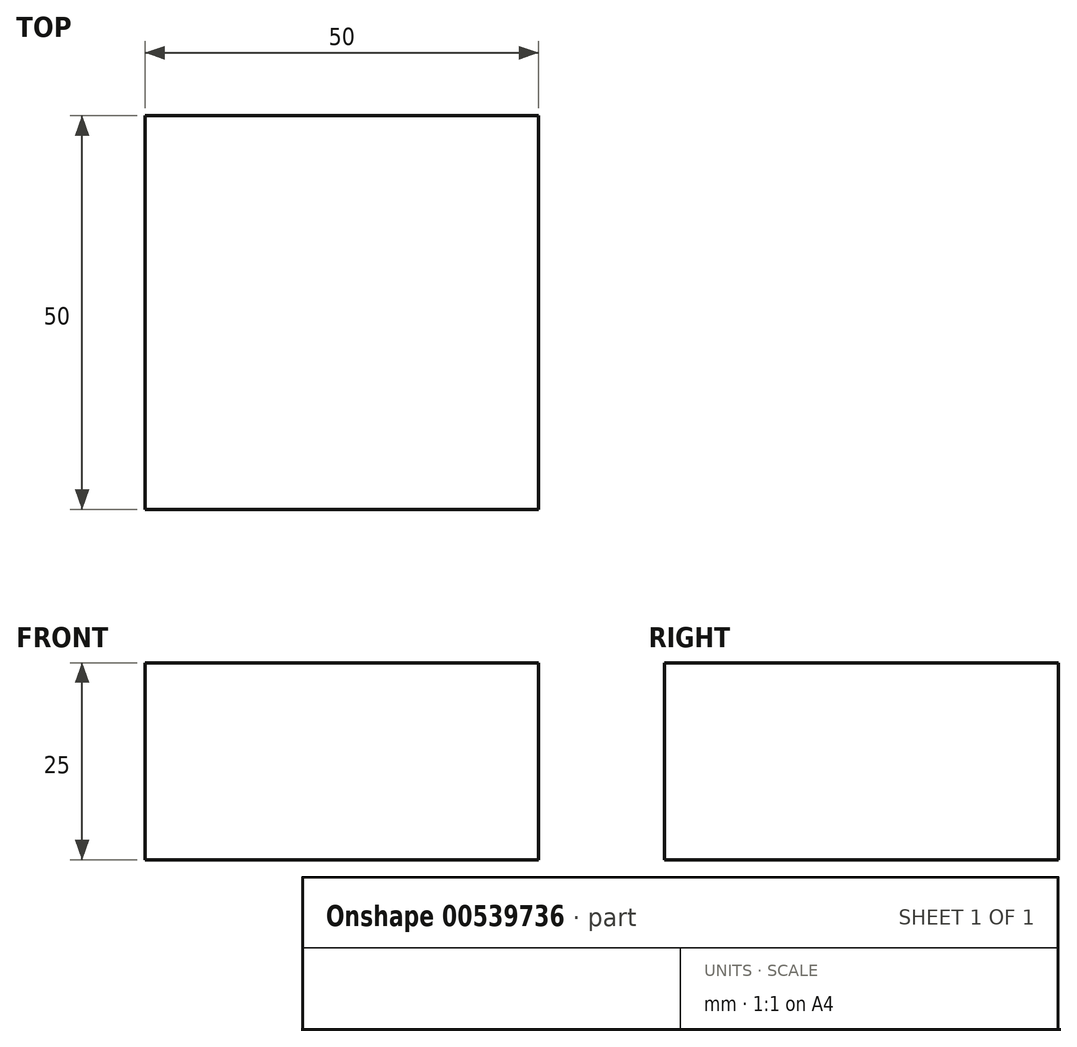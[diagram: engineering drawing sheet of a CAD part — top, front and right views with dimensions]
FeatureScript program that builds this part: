
annotation { "Feature Type Name" : "Feature", "Feature Type Description" : "" }
export const myFeature = defineFeature(function(context is Context, id is Id, definition is map)
    precondition{}
    {
        {
            var Q0;
            Q0=qCreatedBy(makeId("Top.planeOp"),FACE);
            var sketch = newSketch(context, id + "F0", { "sketchPlane" : qUnion([Q0])});
            skLineSegment(sketch, "E0.bottom", {"start": v(0, 0) * mm, "end": v(50, 0) * mm});
            skLineSegment(sketch, "E0.top", {"start": v(0, 50) * mm, "end": v(50, 50) * mm});
            skLineSegment(sketch, "E0.left", {"start": v(0, 0) * mm, "end": v(0, 50) * mm});
            skLineSegment(sketch, "E0.right", {"start": v(50, 0) * mm, "end": v(50, 50) * mm});
            skSolve(sketch);
        }
        {
            var Q0;
            Q0=makeQuery(id+"F0.imprint","IMPRINT",FACE,{"disambiguationData":[TD([[makeQuery(id+"F0.imprint","IMPRINT",EDGE,{"derivedFrom":sQuery(id+"F0.wireOp",EDGE,"E0.bottom")}),1.0]])]});
            extrude(context, id + "F1", {"entities" : qUnion([Q0]), "depth" : 25 * mm, "offsetDistance" : 25 * mm});
        }
    });
